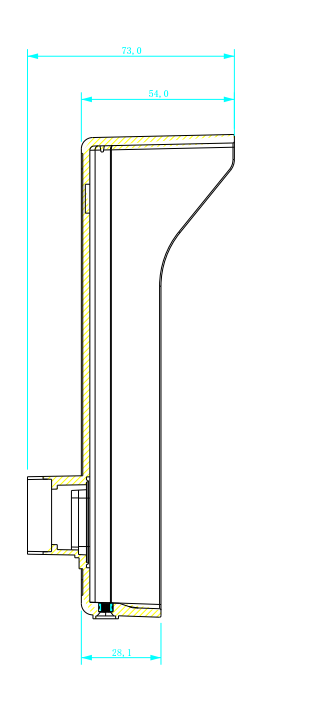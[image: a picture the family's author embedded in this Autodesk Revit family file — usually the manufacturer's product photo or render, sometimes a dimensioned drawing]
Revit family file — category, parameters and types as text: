
# Revit family: SH-46T
name_source: partatom
category: Устройства связи
units: mm (PartAtom-declared; Revit-internal decimal feet)

## family parameters
Всегда вертикально = Нет
На основе рабочей плоскости = Да
Общий = Да
При загрузке вырезать с полостями = Нет
Размер круглого соединителя = Использовать диаметр
Сохранять ориентацию аннотаций = Нет
Тип детали = Нормальный
Точка принадлежности помещению = Нет

## types (1)
- SH-46T
    ADSK_URL документации изделия = http://cdn.bas-ip.com
    ADSK_URL страницы изделия = https://www.bas-ip.ru
    ADSK_Версия Revit = Revit 2020
    ADSK_Единица измерения = шт
    ADSK_Завод-изготовитель = BAS-IP
    ADSK_Классификация нагрузок = Кнопка звонка бесконтактная
    ADSK_Количество фаз = 1
    ADSK_Коэффициент мощности = 0.9
    ADSK_Марка = SH-46T
    ADSK_Наименование = Кнопка звонка бесконтактная SH-46T
    ADSK_Наименование краткое = SH-46T
    ADSK_Напряжение = 12 В
    ADSK_Номинальная мощность = 1 Вт
    ADSK_Полная мощность = 1 В·А
    ADSK_Размер_Длина = 190 мм
    ADSK_Размер_Толщина = 20 мм
    ADSK_Размер_Ширина = 95 мм
    BIM library = https://bimlib.ru
    URL = https://www.bas-ip.ru
    Группа модели = Кнопка звонка бесконтактная SH-46T
    Дополнительно = Возможность изменения (переключения) цвета подсветки, триггерный режим
    Допустимая влажность = 10% – 94%
    Емблеми/надписи = Бесконтактный звонок с возможностью нанесения гравировки на лицевой панели
    Изготовитель = BAS-IP
    Изображение типоразмера = <Нет>
    Корпус = Алюминий
    Кронштейн для врезного монтажа = Есть
    Материал корпуса = Материал серый
    Напряжение питания = +12В (+1%, - 15%)
    Описание = BAS-IP SH-46T — беcконтактный дверной звонок для подключения к видео или аудио домофону
    Отметка по умолчанию = 0 мм
    Размеры = 95×190×19,5 мм
    Расстояние срабатывания = До 15 - 25 см (в зависимости от внешних условий)
    Ресурс работы = Более 100 миллионов нажатий
    Степень защиты = IP68
    Температурный режим = -27 – +60 °C
    Тип кнопки = Бесконтактная
    Цвет = Black, Silver
